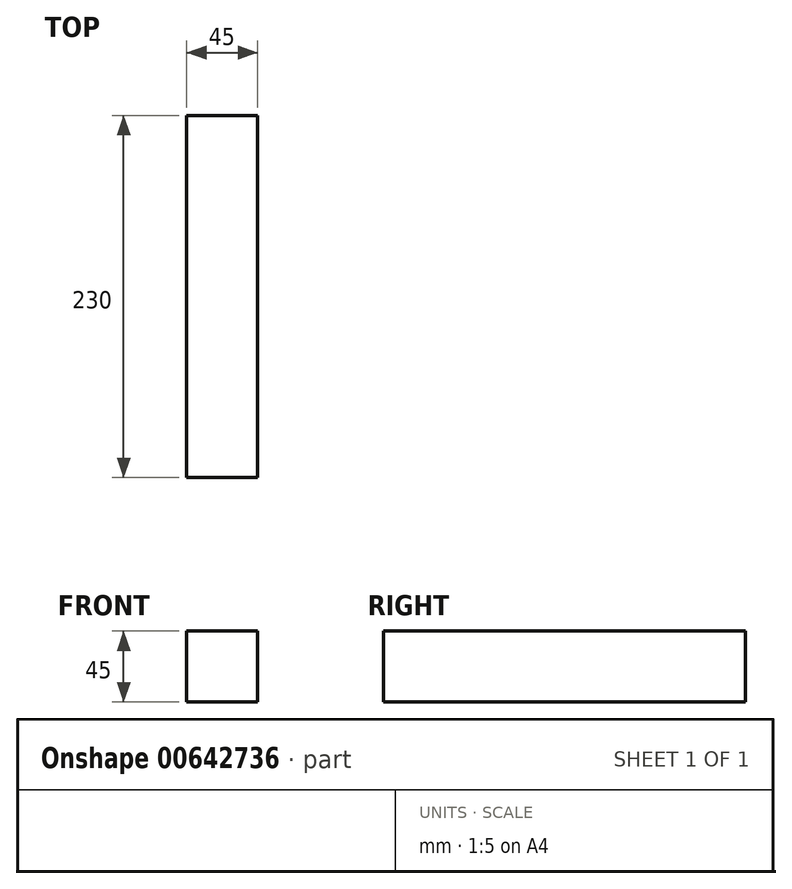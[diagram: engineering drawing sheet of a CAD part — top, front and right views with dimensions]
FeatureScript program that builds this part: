
annotation { "Feature Type Name" : "Feature", "Feature Type Description" : "" }
export const myFeature = defineFeature(function(context is Context, id is Id, definition is map)
    precondition{}
    {
        {
            var Q0;
            Q0=qCreatedBy(makeId("Top.planeOp"),FACE);
            var sketch = newSketch(context, id + "F0", { "sketchPlane" : qUnion([Q0])});
            skLineSegment(sketch, "E0.bottom", {"start": v(0, 0) * mm, "end": v(45, 0) * mm});
            skLineSegment(sketch, "E0.top", {"start": v(0, 230) * mm, "end": v(45, 230) * mm});
            skLineSegment(sketch, "E0.left", {"start": v(0, 0) * mm, "end": v(0, 230) * mm});
            skLineSegment(sketch, "E0.right", {"start": v(45, 0) * mm, "end": v(45, 230) * mm});
            skSolve(sketch);
        }
        {
            var Q0;
            Q0 = qSketchRegion(id + "F0", true);
            extrude(context, id + "F1", {"entities" : qUnion([Q0]), "depth" : 45 * mm, "offsetDistance" : 25 * mm});
        }
    });
